# Revit family: CADS_AIRFLOWdev_AirTerminal_AirBrick_Intake
name_source: partatom
category: Air Terminals
revit_build: Autodesk Revit 2015 (Build: 20160512_0715(x64)
units: mm (PartAtom-declared; Revit-internal decimal feet)

## types (6) — shared parameters
CEApproval = Yes
Default Elevation = 1219 mm
ISO140001 = Yes
ISO90001 = Yes

## per-type parameters (varying)
- Brown: 6MonthlyMaintenance=Visually inspect system, clean the fan and ducting if necessary; A=20 mm  [stored 0.0656168 ft]; AirBrick_Colour=CADS_AirFlow_Brown; AirflowRateRange=0-61; AssetType=Fixed; B=20 mm  [stored 0.0656168 ft]; Color=Brown; Constituents=Brown; Description=204 x 60mm (Brown); DurationUnit=Years; Exclusions=Incorrect Use / Incorrect Installation / Installed by a non-accredited electrician. Customer abuse.; FaceType=LOUVERED; Finish=Matte; FlowControlType=NONE; Grade=Virgin; GrossWeight=0.02 kg; H=61 mm  [stored 0.200131 ft]; HasIntegralControl=No; HasSoundAttenuator=No; HasThermalInsulation=No; Internal_Damper=No; IsExtendedWarranty=No; L=208 mm  [stored 0.682415 ft]; Manufacturer=Airflow Developments Ltd; ManufacturerAddress=Aidelle House
Lancaster Road
Cressex Business Park
High Wycombe
Bucks
HP123QP; ManufacturerTelephone=01494 525252; ManufacturerWebsite=www.airflow.com; Material=Plastic; ModelLabel=204 x 60mm (Brown); ModelReference=51849605; MountingType=FLATFLUSH; NBSCode=90-75-50/370 Air terminals;; NominalHeight=60 mm  [stored 0.19685 ft]; NominalLength=58 mm  [stored 0.190289 ft]; NominalWidth=204 mm  [stored 0.669291 ft]; NumberOfSlots=16; PointOfContact=Airflow Developments Ltd; ProductionYear=2017; Raised_Spigot=Yes; ReplacementCost=8.112; ServiceLifeDuration=10; ServiceLifeType=EXPECTEDSERVICELIFE; Shape=Rectangular; ShippingWeight=0.02 kg; Size=58 x 204 x 60; Uniclass2015=Pr_65_70_46_01; W=64 mm  [stored 0.209974 ft]; WarrantyContent=Replacement of part if faulty; WarrantyGuarantor=Airflow Developments Ltd; WarrantyPeriod=2
- Terracotta: 6MonthlyMaintenance=Visually inspect system, clean the fan and ducting if necessary; A=45 mm  [stored 0.147638 ft]; AirBrick_Colour=CADS_AirFlow_Terracotta; AirflowRateRange=0-61; AssetType=Fixed; B=20 mm  [stored 0.0656168 ft]; Color=Terracotta; Constituents=Terracotta; Description=204 x 60mm (Terracotta); DurationUnit=Years; Exclusions=Incorrect Use / Incorrect Installation / Installed by a non-accredited electrician. Customer abuse.; FaceType=LOUVERED; Finish=Matte; FlowControlType=NONE; Grade=Virgin; GrossWeight=0.02 kg; H=64 mm  [stored 0.209974 ft]; HasIntegralControl=No; HasSoundAttenuator=No; HasThermalInsulation=No; Internal_Damper=No; IsExtendedWarranty=No; L=208 mm  [stored 0.682415 ft]; Manufacturer=Airflow Developments Ltd; ManufacturerAddress=Aidelle House
Lancaster Road
Cressex Business Park
High Wycombe
Bucks
HP123QP; ManufacturerTelephone=01494 525252; ManufacturerWebsite=www.airflow.com; Material=Plastic; ModelLabel=204 x 60mm (Terracotta); ModelReference=52642010; MountingType=FLATFLUSH; NBSCode=90-75-50/370 Air terminals;; NominalHeight=60 mm  [stored 0.19685 ft]; NominalLength=58 mm  [stored 0.190289 ft]; NominalWidth=204 mm  [stored 0.669291 ft]; NumberOfSlots=16; PointOfContact=Airflow Developments Ltd; ProductionYear=2017; Raised_Spigot=No; ReplacementCost=8.112; ServiceLifeDuration=10; ServiceLifeType=EXPECTEDSERVICELIFE; Shape=Rectangular; ShippingWeight=0.02 kg; Size=58 x 204 x 60; Uniclass2015=Pr_65_70_46_01; W=63 mm  [stored 0.206693 ft]; WarrantyContent=Replacement of part if faulty; WarrantyGuarantor=Airflow Developments Ltd; WarrantyPeriod=2
- Beige: 6MonthlyMaintenance=Visually inspect system, clean the fan and ducting if necessary; A=34 mm; AirBrick_Colour=CADS_AirFlow_Beige; AirflowRateRange=0-61; AssetType=Fixed; B=20 mm  [stored 0.0656168 ft]; Color=Beige; Constituents=Beige; Description=204 x 60mm Buff (Beige); DurationUnit=Years; Exclusions=Incorrect Use / Incorrect Installation / Installed by a non-accredited electrician. Customer abuse.; FaceType=LOUVERED; Finish=Matte; FlowControlType=NONE; Grade=Virgin; GrossWeight=0.02 kg; H=64 mm  [stored 0.209974 ft]; HasIntegralControl=No; HasSoundAttenuator=No; HasThermalInsulation=No; Internal_Damper=No; IsExtendedWarranty=No; L=208 mm  [stored 0.682415 ft]; Manufacturer=Airflow Developments Ltd; ManufacturerAddress=Aidelle House
Lancaster Road
Cressex Business Park
High Wycombe
Bucks
HP123QP; ManufacturerTelephone=01494 525252; ManufacturerWebsite=www.airflow.com; Material=Plastic; ModelLabel=204 x 60mm Buff (Beige); ModelReference=52642002; MountingType=FLATFLUSH; NBSCode=90-75-50/370 Air terminals;; NominalHeight=60 mm  [stored 0.19685 ft]; NominalLength=58 mm  [stored 0.190289 ft]; NominalWidth=204 mm  [stored 0.669291 ft]; NumberOfSlots=16; PointOfContact=Airflow Developments Ltd; ProductionYear=2017; Raised_Spigot=No; ReplacementCost=8.112; ServiceLifeDuration=10; ServiceLifeType=EXPECTEDSERVICELIFE; Shape=Rectangular; ShippingWeight=0.02 kg; Size=58 x 204 x 60; Uniclass2015=Pr_65_70_46_01; W=63 mm  [stored 0.206693 ft]; WarrantyContent=Replacement of part if faulty; WarrantyGuarantor=Airflow Developments Ltd; WarrantyPeriod=2
- White: A=34 mm; AirBrick_Colour=CADS_AirFlow_White; B=0 mm  [stored 0 ft]; GrossWeight=0.00 kg; H=54 mm  [stored 0.177165 ft]; HasIntegralControl=Yes; HasSoundAttenuator=Yes; HasThermalInsulation=Yes; Internal_Damper=No; IsExtendedWarranty=Yes; L=200 mm  [stored 0.656168 ft]; NominalHeight=0 mm  [stored 0 ft]; NominalLength=0 mm  [stored 0 ft]; NominalWidth=0 mm  [stored 0 ft]; NumberOfSlots=0; Raised_Spigot=Yes; ShippingWeight=0.00 kg; W=56 mm  [stored 0.183727 ft]
- Terracotta With Internal Damper: 6MonthlyMaintenance=Visually inspect system, clean the fan and ducting if necessary; A=45 mm  [stored 0.147638 ft]; AirBrick_Colour=CADS_AirFlow_Terracotta; AirflowRateRange=0-61; AssetType=Fixed; B=20 mm  [stored 0.0656168 ft]; Color=Terracotta; Constituents=Terracotta; Description=204 x 60mm with internal damper (Terracotta); DurationUnit=Years; Exclusions=Incorrect Use / Incorrect Installation / Installed by a non-accredited electrician. Customer abuse.; FaceType=LOUVERED; Finish=Matte; FlowControlType=DAMPER; Grade=Virgin; GrossWeight=0.02 kg; H=64 mm  [stored 0.209974 ft]; HasIntegralControl=No; HasSoundAttenuator=No; HasThermalInsulation=No; Internal_Damper=Yes; IsExtendedWarranty=No; L=208 mm  [stored 0.682415 ft]; Manufacturer=Airflow Developments Ltd; ManufacturerAddress=Aidelle House
Lancaster Road
Cressex Business Park
High Wycombe
Bucks
HP123QP; ManufacturerTelephone=01494 525252; ManufacturerWebsite=www.airflow.com; Material=Plastic; ModelLabel=204 x 60mm with internal damper (Terracotta); ModelReference=51978702; MountingType=FLATFLUSH; NBSCode=90-75-50/370 Air terminals;; NominalHeight=60 mm  [stored 0.19685 ft]; NominalLength=58 mm  [stored 0.190289 ft]; NominalWidth=204 mm  [stored 0.669291 ft]; NumberOfSlots=16; PointOfContact=Airflow Developments Ltd; ProductionYear=2017; Raised_Spigot=No; ReplacementCost=8.112; ServiceLifeDuration=10; ServiceLifeType=EXPECTEDSERVICELIFE; Shape=Rectangular; ShippingWeight=0.02 kg; Size=58 x 204 x 60; Uniclass2015=Pr_65_70_46_01; W=63 mm  [stored 0.206693 ft]; WarrantyContent=Replacement of part if faulty; WarrantyGuarantor=Airflow Developments Ltd; WarrantyPeriod=2
- White With Internal Damper: 6MonthlyMaintenance=Visually inspect system, clean the fan and ducting if necessary; A=34 mm; AirBrick_Colour=CADS_AirFlow_White; AirflowRateRange=0-61; AssetType=Fixed; B=0 mm  [stored 0 ft]; Color=White; Constituents=White; Description=204 x 60mm with internal damper (White); DurationUnit=Years; Exclusions=Incorrect Use / Incorrect Installation / Installed by a non-accredited electrician. Customer abuse.; FaceType=LOUVERED; Finish=Matte; FlowControlType=DAMPER; Grade=Virgin; GrossWeight=0.02 kg; H=54 mm  [stored 0.177165 ft]; HasIntegralControl=No; HasSoundAttenuator=No; HasThermalInsulation=No; Internal_Damper=Yes; IsExtendedWarranty=No; L=200 mm  [stored 0.656168 ft]; Manufacturer=Airflow Developments Ltd; ManufacturerAddress=Aidelle House
Lancaster Road
Cressex Business Park
High Wycombe
Bucks
HP123QP; ManufacturerTelephone=01494 525252; ManufacturerWebsite=www.airflow.com; Material=Plastic; ModelLabel=204 x 60mm with internal damper (White); ModelReference=51978701; MountingType=FLATFLUSH; NBSCode=90-75-50/370 Air terminals;; NominalHeight=60 mm  [stored 0.19685 ft]; NominalLength=58 mm  [stored 0.190289 ft]; NominalWidth=204 mm  [stored 0.669291 ft]; NumberOfSlots=27; PointOfContact=Airflow Developments Ltd; ProductionYear=2017; Raised_Spigot=Yes; ReplacementCost=8.112; ServiceLifeDuration=10; ServiceLifeType=EXPECTEDSERVICELIFE; Shape=Rectangular; ShippingWeight=0.02 kg; Size=58 x 204 x 60; Uniclass2015=Pr_65_70_46_01; W=56 mm  [stored 0.183727 ft]; WarrantyContent=Replacement of part if faulty; WarrantyGuarantor=Airflow Developments Ltd; WarrantyPeriod=2

note: [stored X ft] marks values corroborated as IEEE doubles in the binary element streams (Revit-internal decimal feet)

## geometry (parser evidence)
native form markers: Blend x14, Sweep x3
no freeform markers — native parametric forms only
